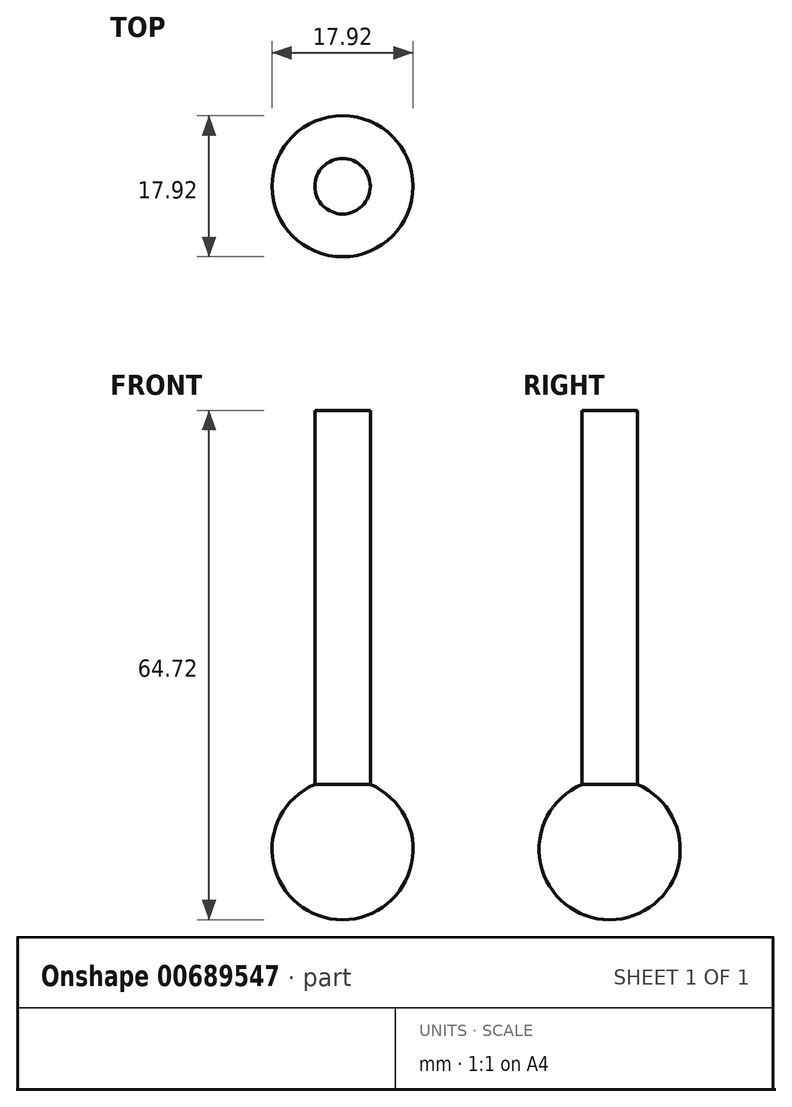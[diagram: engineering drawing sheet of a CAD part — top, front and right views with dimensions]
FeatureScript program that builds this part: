
annotation { "Feature Type Name" : "Feature", "Feature Type Description" : "" }
export const myFeature = defineFeature(function(context is Context, id is Id, definition is map)
    precondition{}
    {
        {
            var Q0;
            Q0=qCreatedBy(makeId("Front.planeOp"),FACE);
            var sketch = newSketch(context, id + "F0", { "sketchPlane" : qUnion([Q0])});
            skCircle(sketch, "E0", {"center": v(0, 0) * mm, "radius": 8.96 * mm});
            skLineSegment(sketch, "E1.left", {"start": v(-3.52, 0) * mm, "end": v(-3.52, 55.76) * mm});
            skLineSegment(sketch, "E2.MirrorCS", {"start": v(3.52, 0) * mm, "end": v(3.52, 55.76) * mm});
            skLineSegment(sketch, "E3", {"start": v(-3.52, 55.76) * mm, "end": v(3.52, 55.76) * mm});
            skLineSegment(sketch, "E4", {"start": v(-3.52, 0) * mm, "end": v(3.52, 0) * mm});
            skLineSegment(sketch, "E5", {"start": v(0, 55.76) * mm, "end": v(0, -8.96) * mm});
            skSolve(sketch);
        }
        {
            var Q0;
            {var subQ0=sQuery(id+"F0.wireOp",EDGE,"E1.left");var subQ1=sQuery(id+"F0.wireOp",EDGE,"E0");var subQ2=makeQuery(id+"F0.imprint","INTERSECT",VERTEX,{"derivedFrom":[subQ1,subQ0]});Q0=makeQuery(id+"F0.imprint","IMPRINT",FACE,{"disambiguationData":[TD([[makeQuery(id+"F0.imprint","IMPRINT",EDGE,{"disambiguationData":[TD([[subQ2,1.0]])],"derivedFrom":subQ1}),-1.0]])]});}
            var Q1;
            {var subQ0=sQuery(id+"F0.wireOp",EDGE,"E5");var subQ1=sQuery(id+"F0.wireOp",EDGE,"E0");var subQ2=makeQuery(id+"F0.imprint","INTERSECT",VERTEX,{"disambiguationData":[OD(0.0)],"derivedFrom":[subQ1,subQ0]});Q1=makeQuery(id+"F0.imprint","IMPRINT",FACE,{"disambiguationData":[TD([[makeQuery(id+"F0.imprint","IMPRINT",EDGE,{"disambiguationData":[TD([[subQ2,1.0]])],"derivedFrom":subQ1}),1.0]])]});}
            var Q2;
            {var subQ0=sQuery(id+"F0.wireOp",EDGE,"E1.left");var subQ1=sQuery(id+"F0.wireOp",EDGE,"E0");var subQ2=makeQuery(id+"F0.imprint","INTERSECT",VERTEX,{"derivedFrom":[subQ1,subQ0]});Q2=makeQuery(id+"F0.imprint","IMPRINT",FACE,{"disambiguationData":[TD([[makeQuery(id+"F0.imprint","IMPRINT",EDGE,{"disambiguationData":[TD([[subQ2,1.0]])],"derivedFrom":subQ1}),1.0]])]});}
            var Q3;
            Q3=sQuery(id+"F0.wireOp",EDGE,"E5");
            revolve(context, id + "F1", {"entities" : qUnion([Q0, Q1, Q2]), "axis" : qUnion([Q3]), "revolveType" : RevolveType.FULL});
        }
    });
